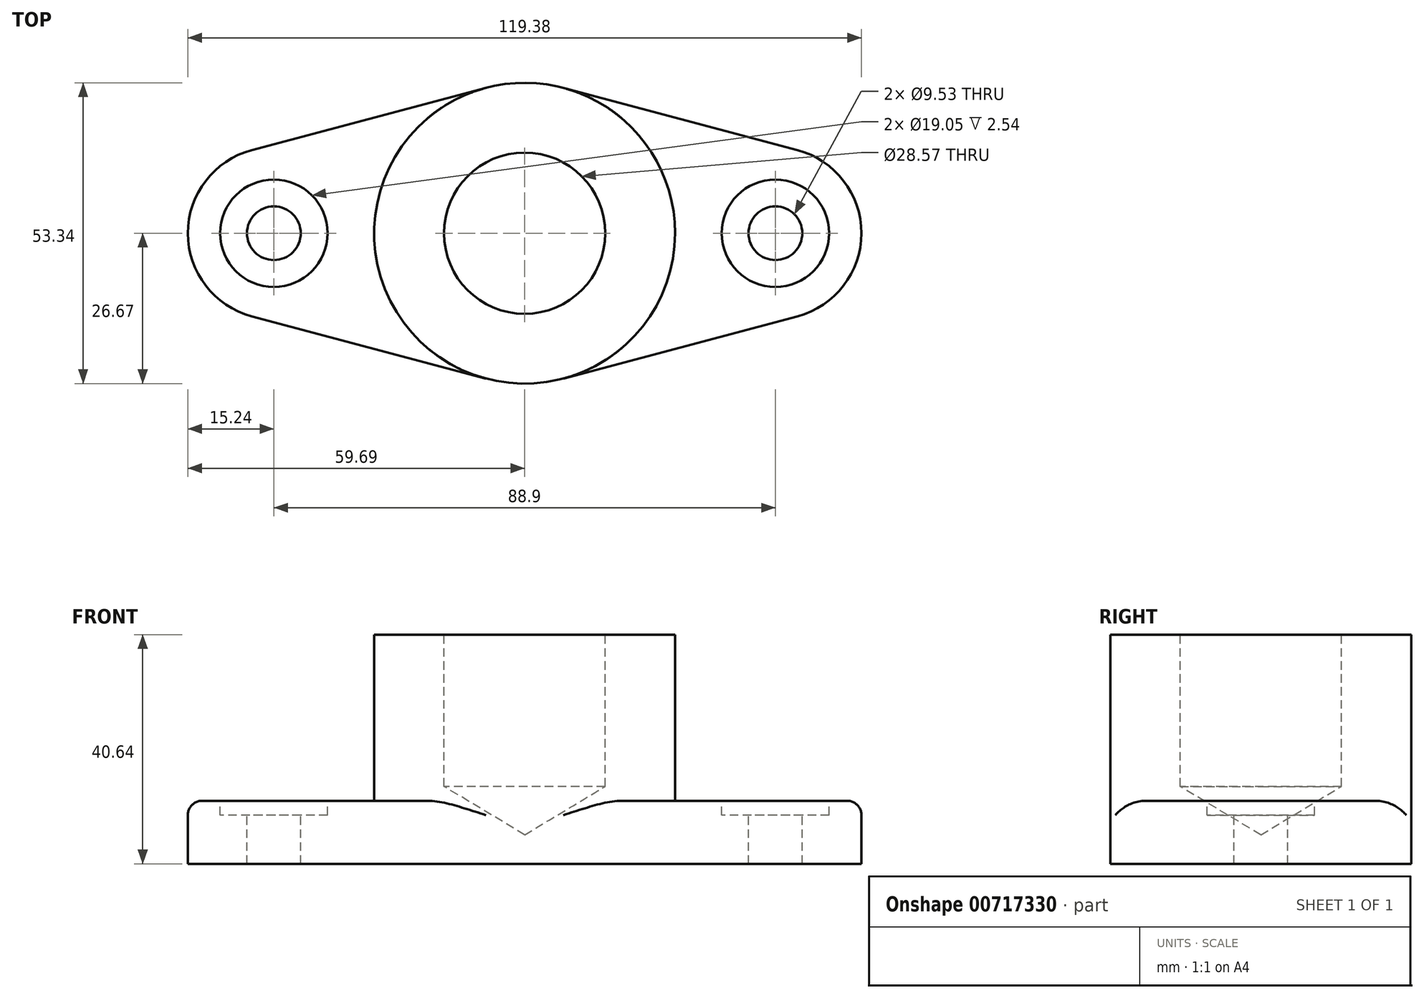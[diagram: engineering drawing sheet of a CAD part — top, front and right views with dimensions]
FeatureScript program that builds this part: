
annotation { "Feature Type Name" : "Feature", "Feature Type Description" : "" }
export const myFeature = defineFeature(function(context is Context, id is Id, definition is map)
    precondition{}
    {
        {
            var Q0;
            Q0=qCreatedBy(makeId("Top.planeOp"),FACE);
            var sketch = newSketch(context, id + "F0", { "sketchPlane" : qUnion([Q0])});
            skLineSegment(sketch, "E0", {"start": v(-48.37, 14.73) * mm, "end": v(-6.86, 25.77) * mm});
            skLineSegment(sketch, "E1", {"start": v(6.86, 25.77) * mm, "end": v(48.37, 14.73) * mm});
            skLineSegment(sketch, "E2", {"start": v(-48.37, -14.73) * mm, "end": v(-6.86, -25.77) * mm});
            skLineSegment(sketch, "E3", {"start": v(6.86, -25.77) * mm, "end": v(48.37, -14.73) * mm});
            skArc(sketch, "E4.filletArc", {"start": v(48.37, -14.73) * mm, "mid": v(59.69, 0) * mm, "end": v(48.37, 14.73) * mm});
            skArc(sketch, "E5.filletArc", {"start": v(-48.37, 14.73) * mm, "mid": v(-59.7, 0) * mm, "end": v(-48.37, -14.73) * mm});
            skArc(sketch, "E6", {"start": v(-6.86, -25.77) * mm, "mid": v(0, -26.67) * mm, "end": v(6.86, -25.77) * mm});
            skArc(sketch, "E7.trimOffspring", {"start": v(6.86, 25.77) * mm, "mid": v(0, 26.67) * mm, "end": v(-6.86, 25.77) * mm});
            skSolve(sketch);
        }
        {
            var Q0;
            Q0 = qSketchRegion(id + "F0", true);
            extrude(context, id + "F1", {"entities" : qUnion([Q0]), "depth" : 11.18 * mm, "offsetDistance" : 25.4 * mm});
        }
        {
            var Q0;
            Q0=makeQuery(id+"F1.opExtrude","CAP_FACE",FACE,{"disambiguationData":[OSD([sQuery(id+"F0.wireOp",EDGE,"E0"),sQuery(id+"F0.wireOp",EDGE,"E1"),sQuery(id+"F0.wireOp",EDGE,"E2"),sQuery(id+"F0.wireOp",EDGE,"E3"),sQuery(id+"F0.wireOp",EDGE,"E4.filletArc"),sQuery(id+"F0.wireOp",EDGE,"E5.filletArc"),sQuery(id+"F0.wireOp",EDGE,"E6"),sQuery(id+"F0.wireOp",EDGE,"E7.trimOffspring")])],"isStart":false});
            var sketch = newSketch(context, id + "F2", { "sketchPlane" : qUnion([Q0])});
            skCircle(sketch, "E8", {"center": v(0, 0) * mm, "radius": 26.67 * mm});
            skSolve(sketch);
        }
        {
            var Q0;
            Q0 = qSketchRegion(id + "F2", true);
            extrude(context, id + "F3", {"entities" : qUnion([Q0]), "operationType" : NewBodyOperationType.ADD, "depth" : 29.46 * mm, "offsetDistance" : 25 * mm});
        }
        {
            var Q0;
            Q0=makeQuery(id+"F3.opExtrude","CAP_FACE",FACE,{"disambiguationData":[OSD([sQuery(id+"F2.wireOp",EDGE,"E8")])],"isStart":false});
            var sketch = newSketch(context, id + "F4", { "sketchPlane" : qUnion([Q0])});
            skPoint(sketch, "E9", {"position": v(0, 0) * mm});
            skSolve(sketch);
        }
        {
            var Q0;
            Q0=sQuery(id+"F4.wireOp",VERTEX,"E9");
            var Q1;
            Q1=makeQuery(id+"F1.opExtrude","SWEPT_BODY",BODY,{"disambiguationData":[OSD([sQuery(id+"F0.wireOp",EDGE,"E0"),sQuery(id+"F0.wireOp",EDGE,"E1"),sQuery(id+"F0.wireOp",EDGE,"E2"),sQuery(id+"F0.wireOp",EDGE,"E3"),sQuery(id+"F0.wireOp",EDGE,"E4.filletArc"),sQuery(id+"F0.wireOp",EDGE,"E5.filletArc"),sQuery(id+"F0.wireOp",EDGE,"E6"),sQuery(id+"F0.wireOp",EDGE,"E7.trimOffspring")])]});
            hole(context, id + "F5", {"style" : HoleStyle.SIMPLE, "endStyle" : HoleEndStyle.BLIND, "holeDiameter" : 28.57 * mm, "majorDiameter" : 6.35 * mm, "holeDepth" : 26.92 * mm, "isTappedThrough" : true, "tappedDepth" : 12.7 * mm, "tapClearance" : 3, "startFromSketch" : true, "locations" : qUnion([Q0]), "scope" : qUnion([Q1])});
        }
        {
            var Q0;
            {var subQ0=sQuery(id+"F0.wireOp",EDGE,"E6");var subQ1=sQuery(id+"F0.wireOp",EDGE,"E5.filletArc");var subQ2=sQuery(id+"F0.wireOp",EDGE,"E2");var subQ3=sQuery(id+"F0.wireOp",EDGE,"E0");var subQ4=sQuery(id+"F0.wireOp",EDGE,"E7.trimOffspring");Q0=makeQuery(id+"F7402xe7Un7UO8w_1.boolean.opBoolean","SPLIT",FACE,{"disambiguationData":[TD([makeQuery(id+"F1.opExtrude","SWEPT_FACE",FACE,{"disambiguationData":[OSD([subQ3])]})])],"derivedFrom":makeQuery(id+"F1.opExtrude","CAP_FACE",FACE,{"disambiguationData":[OSD([subQ3,sQuery(id+"F0.wireOp",EDGE,"E1"),subQ2,sQuery(id+"F0.wireOp",EDGE,"E3"),sQuery(id+"F0.wireOp",EDGE,"E4.filletArc"),subQ1,subQ0,subQ4])],"isStart":false})});}
            var sketch = newSketch(context, id + "F6", { "sketchPlane" : qUnion([Q0])});
            skPoint(sketch, "E10", {"position": v(-44.45, 0) * mm});
            skPoint(sketch, "E11", {"position": v(44.45, 0) * mm});
            skSolve(sketch);
        }
        {
            var Q0;
            Q0=sQuery(id+"F6.wireOp",VERTEX,"E10");
            var Q1;
            Q1=sQuery(id+"F6.wireOp",VERTEX,"E11");
            var Q2;
            Q2=makeQuery(id+"F1.opExtrude","SWEPT_BODY",BODY,{"disambiguationData":[OSD([sQuery(id+"F0.wireOp",EDGE,"E0"),sQuery(id+"F0.wireOp",EDGE,"E1"),sQuery(id+"F0.wireOp",EDGE,"E2"),sQuery(id+"F0.wireOp",EDGE,"E3"),sQuery(id+"F0.wireOp",EDGE,"E4.filletArc"),sQuery(id+"F0.wireOp",EDGE,"E5.filletArc"),sQuery(id+"F0.wireOp",EDGE,"E6"),sQuery(id+"F0.wireOp",EDGE,"E7.trimOffspring")])]});
            hole(context, id + "F7", {"style" : HoleStyle.C_BORE, "endStyle" : HoleEndStyle.THROUGH, "holeDiameter" : 9.52 * mm, "cBoreDiameter" : 19.05 * mm, "cBoreDepth" : 2.54 * mm, "majorDiameter" : 6.35 * mm, "isTappedThrough" : true, "tappedDepth" : 12.7 * mm, "tapClearance" : 3, "startFromSketch" : true, "locations" : qUnion([Q0, Q1]), "scope" : qUnion([Q2])});
        }
        {
            var Q0;
            Q0=makeQuery(id+"F1.opExtrude","CAP_EDGE",EDGE,{"disambiguationData":[OSD([sQuery(id+"F0.wireOp",EDGE,"E2")])],"isStart":false});
            var Q1;
            Q1=makeQuery(id+"F1.opExtrude","CAP_EDGE",EDGE,{"disambiguationData":[OSD([sQuery(id+"F0.wireOp",EDGE,"E3")])],"isStart":false});
            var Q2;
            {var subQ2=sQuery(id+"F0.wireOp",EDGE,"E1");var subQ4=sQuery(id+"F2.wireOp",EDGE,"E8");Q2=makeQuery(id+"F7402xe7Un7UO8w_1.boolean.opBoolean","SPLIT",EDGE,{"disambiguationData":[TD([makeQuery(id+"F1.opExtrude","SWEPT_FACE",FACE,{"disambiguationData":[OSD([subQ2])]})])],"derivedFrom":makeQuery(id+"F7402xe7Un7UO8w_1.opExtrude","CAP_EDGE",EDGE,{"disambiguationData":[OSD([subQ4])],"isStart":true})});}
            var Q3;
            {var subQ3=sQuery(id+"F0.wireOp",EDGE,"E0");var subQ4=sQuery(id+"F2.wireOp",EDGE,"E8");Q3=makeQuery(id+"F7402xe7Un7UO8w_1.boolean.opBoolean","SPLIT",EDGE,{"disambiguationData":[TD([makeQuery(id+"F1.opExtrude","SWEPT_FACE",FACE,{"disambiguationData":[OSD([subQ3])]})])],"derivedFrom":makeQuery(id+"F7402xe7Un7UO8w_1.opExtrude","CAP_EDGE",EDGE,{"disambiguationData":[OSD([subQ4])],"isStart":true})});}
            var Q4;
            Q4=makeQuery(id+"F1.opExtrude","SWEPT_EDGE",EDGE,{"disambiguationData":[OSD([sQuery(id+"F0.wireOp",EDGE,"E0"),sQuery(id+"F0.wireOp",EDGE,"E5.filletArc")])]});
            var Q5;
            Q5=makeQuery(id+"F1.opExtrude","SWEPT_EDGE",EDGE,{"disambiguationData":[OSD([sQuery(id+"F0.wireOp",EDGE,"E0"),sQuery(id+"F0.wireOp",EDGE,"E7.trimOffspring")])]});
            var Q6;
            Q6=makeQuery(id+"F1.opExtrude","SWEPT_EDGE",EDGE,{"disambiguationData":[OSD([sQuery(id+"F0.wireOp",EDGE,"E1"),sQuery(id+"F0.wireOp",EDGE,"E7.trimOffspring")])]});
            fillet(context, id + "F8", {"entities" : qUnion([Q0, Q1, Q2, Q3, Q4, Q5, Q6]), "radius" : 2.54 * mm, "tangentPropagation" : true, "allowEdgeOverflow" : false});
        }
    });
